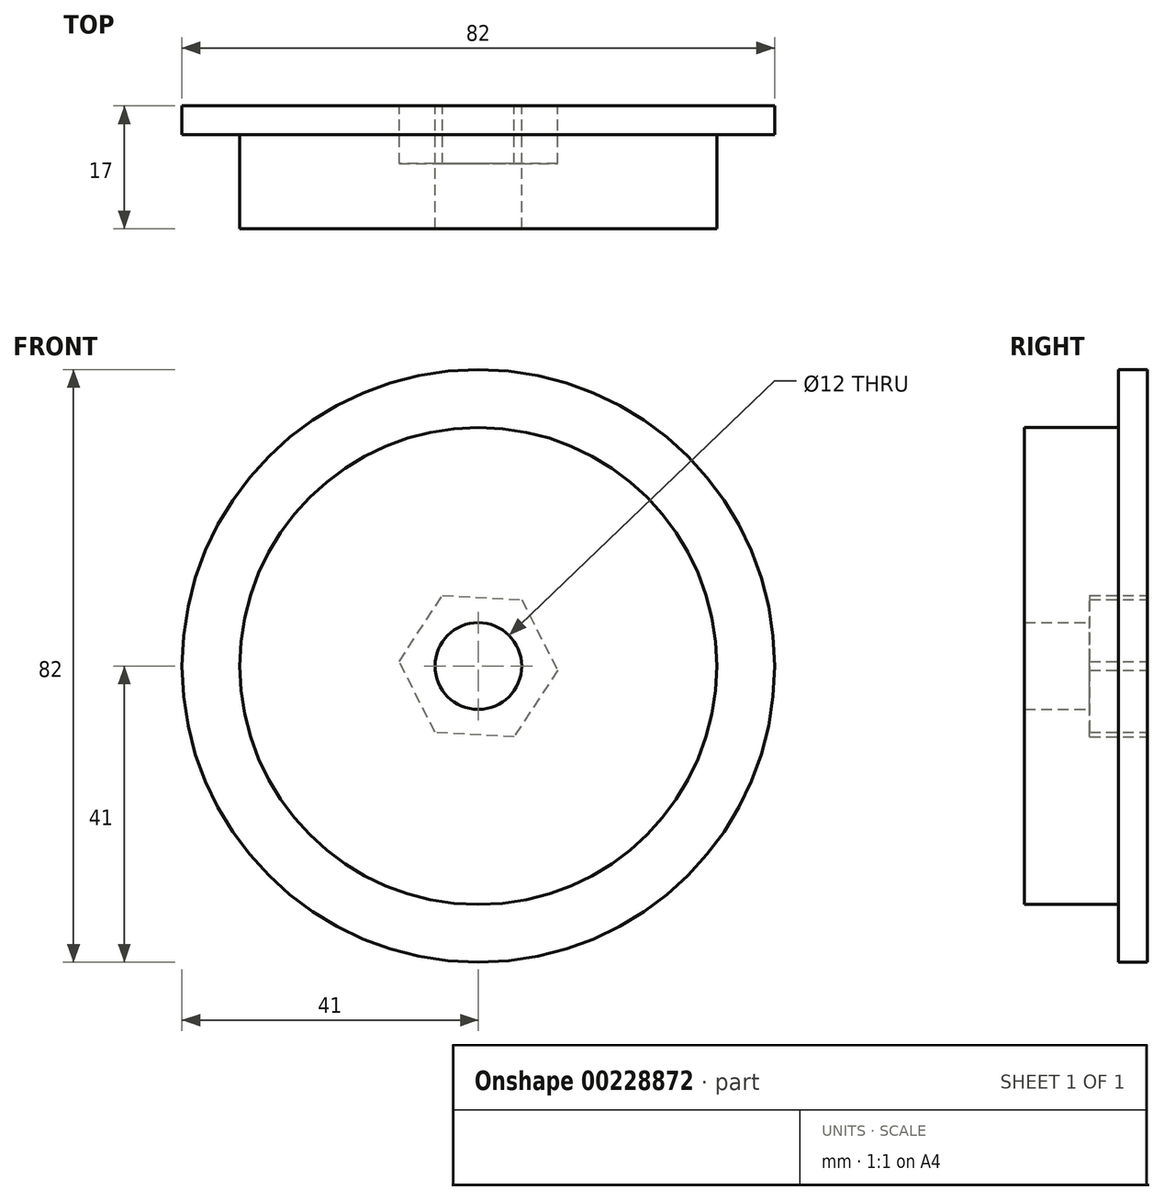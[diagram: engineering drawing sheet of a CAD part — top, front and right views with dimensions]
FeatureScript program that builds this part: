
annotation { "Feature Type Name" : "Feature", "Feature Type Description" : "" }
export const myFeature = defineFeature(function(context is Context, id is Id, definition is map)
    precondition{}
    {
        {
            var Q0;
            Q0=qCreatedBy(makeId("Front.planeOp"),FACE);
            var sketch = newSketch(context, id + "F0", { "sketchPlane" : qUnion([Q0])});
            skCircle(sketch, "E0", {"center": v(0, 0) * mm, "radius": 41 * mm});
            skCircle(sketch, "E1", {"center": v(0, 0) * mm, "radius": 33 * mm});
            skSolve(sketch);
        }
        {
            var Q0;
            Q0=qCreatedBy(makeId("Front.planeOp"),FACE);
            var sketch = newSketch(context, id + "F1", { "sketchPlane" : qUnion([Q0])});
            skCircle(sketch, "E2", {"center": v(0, 0) * mm, "radius": 33 * mm});
            skCircle(sketch, "E3", {"center": v(0, 0) * mm, "radius": 6 * mm});
            skSolve(sketch);
        }
        {
            var Q0;
            Q0=makeQuery(id+"F0.imprint","IMPRINT",FACE,{"disambiguationData":[TD([[makeQuery(id+"F0.imprint","IMPRINT",EDGE,{"derivedFrom":sQuery(id+"F0.wireOp",EDGE,"E0")}),1.0]])]});
            extrude(context, id + "F2", {"entities" : qUnion([Q0]), "depth" : 4 * mm});
        }
        {
            var Q0;
            Q0=makeQuery(id+"F1.imprint","IMPRINT",FACE,{"disambiguationData":[TD([[makeQuery(id+"F1.imprint","IMPRINT",EDGE,{"derivedFrom":sQuery(id+"F1.wireOp",EDGE,"E2")}),1.0]])]});
            extrude(context, id + "F3", {"entities" : qUnion([Q0]), "operationType" : NewBodyOperationType.ADD, "depth" : 17 * mm});
        }
        {
            var Q0;
            Q0=qCreatedBy(makeId("Front.planeOp"),FACE);
            var sketch = newSketch(context, id + "F4", { "sketchPlane" : qUnion([Q0])});
            skLineSegment(sketch, "E4.0", {"start": v(-6, -9.18) * mm, "end": v(-10.95, 0.6) * mm});
            skLineSegment(sketch, "E4.1", {"start": v(-10.95, 0.6) * mm, "end": v(-4.95, 9.79) * mm});
            skLineSegment(sketch, "E4.2", {"start": v(-4.95, 9.79) * mm, "end": v(6, 9.18) * mm});
            skLineSegment(sketch, "E4.3", {"start": v(6, 9.18) * mm, "end": v(10.95, -0.6) * mm});
            skLineSegment(sketch, "E4.4", {"start": v(10.95, -0.6) * mm, "end": v(4.95, -9.79) * mm});
            skLineSegment(sketch, "E4.5", {"start": v(4.95, -9.79) * mm, "end": v(-6, -9.18) * mm});
            skPoint(sketch, "E4.0.midPoint", {"position": v(-8.48, -4.29) * mm});
            skCircle(sketch, "E5", {"center": v(0, 0) * mm, "radius": 6 * mm});
            skSolve(sketch);
        }
        {
            var Q0;
            Q0=makeQuery(id+"F4.imprint","IMPRINT",FACE,{"disambiguationData":[TD([[makeQuery(id+"F4.imprint","IMPRINT",EDGE,{"derivedFrom":sQuery(id+"F4.wireOp",EDGE,"E4.0")}),-1.0]])]});
            extrude(context, id + "F5", {"entities" : qUnion([Q0]), "operationType" : NewBodyOperationType.REMOVE, "depth" : 8 * mm});
        }
    });
